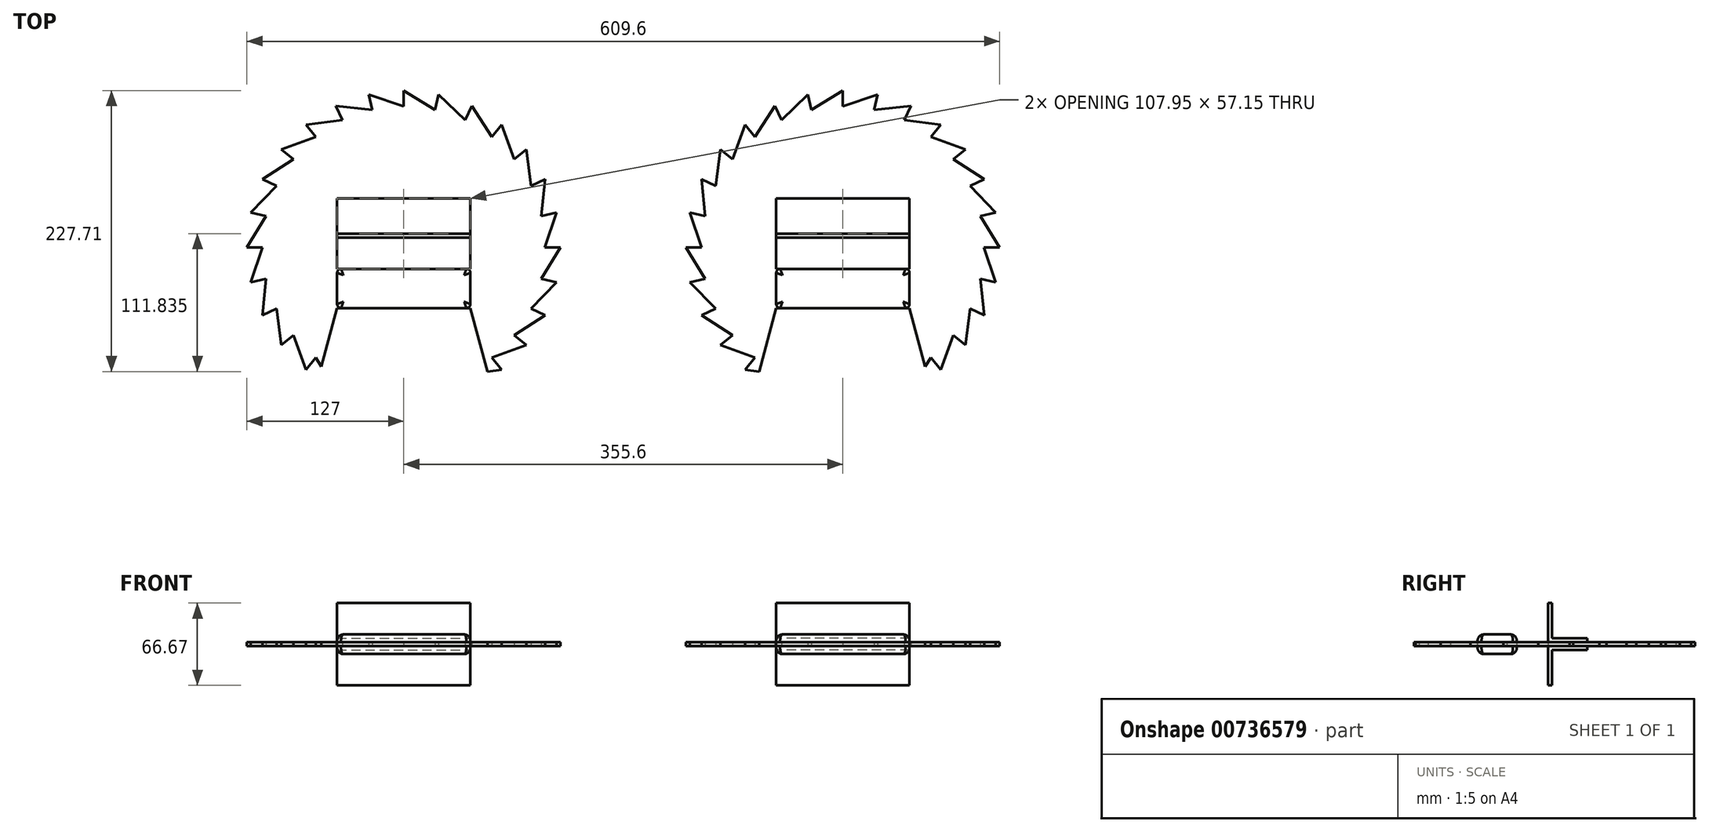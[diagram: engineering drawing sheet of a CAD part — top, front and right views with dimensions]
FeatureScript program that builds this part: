
annotation { "Feature Type Name" : "Feature", "Feature Type Description" : "" }
export const myFeature = defineFeature(function(context is Context, id is Id, definition is map)
    precondition{}
    {
        {
            var Q0;
            Q0=qCreatedBy(makeId("Top.planeOp"),FACE);
            var sketch = newSketch(context, id + "F0", { "sketchPlane" : qUnion([Q0])});
            skArc(sketch, "E0", {"start": v(-123.82, -114.96) * mm, "mid": v(-123.26, -114.7) * mm, "end": v(-122.7, -114.42) * mm, "construction": true});
            skLineSegment(sketch, "E1", {"start": v(-177.8, 114.3) * mm, "end": v(-177.8, 127) * mm});
            skLineSegment(sketch, "E2", {"start": v(-206.06, 123.82) * mm, "end": v(-203.23, 111.43) * mm});
            skLineSegment(sketch, "E3", {"start": v(-232.9, 114.42) * mm, "end": v(-227.4, 102.98) * mm});
            skLineSegment(sketch, "E4", {"start": v(-256.98, 99.3) * mm, "end": v(-249.06, 89.36) * mm});
            skLineSegment(sketch, "E5", {"start": v(-277.1, 79.18) * mm, "end": v(-267.16, 71.27) * mm});
            skLineSegment(sketch, "E6", {"start": v(-292.22, 55.1) * mm, "end": v(-280.78, 49.6) * mm});
            skLineSegment(sketch, "E7", {"start": v(-301.62, 28.26) * mm, "end": v(-289.23, 25.44) * mm});
            skLineSegment(sketch, "E8", {"start": v(-304.8, 0) * mm, "end": v(-292.1, 0) * mm});
            skLineSegment(sketch, "E9", {"start": v(-301.62, -28.26) * mm, "end": v(-289.23, -25.43) * mm});
            skLineSegment(sketch, "E10", {"start": v(-292.22, -55.1) * mm, "end": v(-280.78, -49.6) * mm});
            skLineSegment(sketch, "E11", {"start": v(-277.1, -79.18) * mm, "end": v(-267.17, -71.26) * mm});
            skLineSegment(sketch, "E12", {"start": v(-149.54, 123.82) * mm, "end": v(-152.37, 111.43) * mm});
            skLineSegment(sketch, "E13", {"start": v(-122.7, 114.42) * mm, "end": v(-128.2, 102.98) * mm});
            skLineSegment(sketch, "E14", {"start": v(-98.62, 99.3) * mm, "end": v(-106.54, 89.36) * mm});
            skLineSegment(sketch, "E15", {"start": v(-78.5, 79.18) * mm, "end": v(-88.44, 71.27) * mm});
            skLineSegment(sketch, "E16", {"start": v(-63.38, 55.1) * mm, "end": v(-74.82, 49.6) * mm});
            skLineSegment(sketch, "E17", {"start": v(-53.98, 28.26) * mm, "end": v(-66.37, 25.44) * mm});
            skLineSegment(sketch, "E18", {"start": v(-50.8, 0) * mm, "end": v(-63.5, 0) * mm});
            skLineSegment(sketch, "E19", {"start": v(-53.98, -28.26) * mm, "end": v(-66.37, -25.43) * mm});
            skLineSegment(sketch, "E20", {"start": v(-63.38, -55.1) * mm, "end": v(-74.82, -49.6) * mm});
            skLineSegment(sketch, "E21", {"start": v(-78.5, -79.18) * mm, "end": v(-88.43, -71.26) * mm});
            skLineSegment(sketch, "E22", {"start": v(-98.61, -99.3) * mm, "end": v(-106.53, -89.36) * mm});
            skLineSegment(sketch, "E23", {"start": v(-256.99, -99.3) * mm, "end": v(-249.07, -89.36) * mm});
            skLineSegment(sketch, "E24", {"start": v(-122.7, -114.42) * mm, "end": v(-128.2, -102.98) * mm, "construction": true});
            skLineSegment(sketch, "E25", {"start": v(-110.02, -100.71) * mm, "end": v(-98.61, -99.3) * mm});
            skLineSegment(sketch, "E26", {"start": v(-106.53, -89.36) * mm, "end": v(-78.5, -79.18) * mm});
            skLineSegment(sketch, "E27", {"start": v(-88.43, -71.26) * mm, "end": v(-63.38, -55.1) * mm});
            skLineSegment(sketch, "E28", {"start": v(-74.82, -49.6) * mm, "end": v(-53.98, -28.26) * mm});
            skLineSegment(sketch, "E29", {"start": v(-66.37, -25.43) * mm, "end": v(-50.8, 0) * mm});
            skLineSegment(sketch, "E30", {"start": v(-63.5, 0) * mm, "end": v(-53.98, 28.26) * mm});
            skLineSegment(sketch, "E31", {"start": v(-66.37, 25.44) * mm, "end": v(-63.38, 55.1) * mm});
            skLineSegment(sketch, "E32", {"start": v(-74.82, 49.6) * mm, "end": v(-78.5, 79.18) * mm});
            skLineSegment(sketch, "E33", {"start": v(-88.44, 71.27) * mm, "end": v(-98.62, 99.3) * mm});
            skLineSegment(sketch, "E34", {"start": v(-106.54, 89.36) * mm, "end": v(-122.7, 114.42) * mm});
            skLineSegment(sketch, "E35", {"start": v(-128.2, 102.98) * mm, "end": v(-149.54, 123.82) * mm});
            skLineSegment(sketch, "E36", {"start": v(-152.37, 111.43) * mm, "end": v(-177.8, 127) * mm});
            skLineSegment(sketch, "E37", {"start": v(-177.8, 114.3) * mm, "end": v(-206.06, 123.82) * mm});
            skLineSegment(sketch, "E38", {"start": v(-203.23, 111.43) * mm, "end": v(-232.9, 114.42) * mm});
            skLineSegment(sketch, "E39", {"start": v(-227.4, 102.98) * mm, "end": v(-256.98, 99.3) * mm});
            skLineSegment(sketch, "E40", {"start": v(-249.06, 89.36) * mm, "end": v(-277.1, 79.18) * mm});
            skLineSegment(sketch, "E41", {"start": v(-267.16, 71.27) * mm, "end": v(-292.22, 55.1) * mm});
            skLineSegment(sketch, "E42", {"start": v(-280.78, 49.6) * mm, "end": v(-301.62, 28.26) * mm});
            skLineSegment(sketch, "E43", {"start": v(-289.23, 25.44) * mm, "end": v(-304.8, 0) * mm});
            skLineSegment(sketch, "E44", {"start": v(-292.1, 0) * mm, "end": v(-301.62, -28.26) * mm});
            skLineSegment(sketch, "E45", {"start": v(-289.23, -25.43) * mm, "end": v(-292.22, -55.1) * mm});
            skLineSegment(sketch, "E46", {"start": v(-280.78, -49.6) * mm, "end": v(-277.1, -79.18) * mm});
            skLineSegment(sketch, "E47", {"start": v(-267.17, -71.26) * mm, "end": v(-256.99, -99.3) * mm});
            skLineSegment(sketch, "E48", {"start": v(-249.07, -89.36) * mm, "end": v(-244.45, -96.52) * mm});
            skLineSegment(sketch, "E49", {"start": v(-231.78, 7.95) * mm, "end": v(-123.83, 7.95) * mm});
            skLineSegment(sketch, "E50", {"start": v(-231.78, 7.95) * mm, "end": v(-231.78, -17.45) * mm});
            skLineSegment(sketch, "E51", {"start": v(-123.83, 7.95) * mm, "end": v(-123.83, -17.45) * mm});
            skPoint(sketch, "E52", {"position": v(-123.83, -102.43) * mm});
            skLineSegment(sketch, "E53", {"start": v(-231.78, -17.45) * mm, "end": v(-123.83, -17.45) * mm});
            skLineSegment(sketch, "E54", {"start": v(-231.78, -49.2) * mm, "end": v(-123.83, -49.2) * mm});
            skLineSegment(sketch, "E55", {"start": v(-123.83, -49.2) * mm, "end": v(-97.38, -147.88) * mm});
            skLineSegment(sketch, "E56", {"start": v(-231.78, -49.2) * mm, "end": v(-265.1, -173.6) * mm});
            skPoint(sketch, "E57", {"position": v(-244.45, -96.52) * mm});
            skPoint(sketch, "E58", {"position": v(-110.02, -100.71) * mm});
            skSolve(sketch);
        }
        {
            var Q0;
            Q0=makeQuery(id+"F0.imprint","IMPRINT",FACE,{"disambiguationData":[TD([[makeQuery(id+"F0.imprint","IMPRINT",EDGE,{"derivedFrom":sQuery(id+"F0.wireOp",EDGE,"E1")}),-1.0]])]});
            extrude(context, id + "F1", {"entities" : qUnion([Q0]), "depth" : 3.17 * mm, "offsetDistance" : 25.4 * mm});
        }
        {
            var Q0;
            Q0=qCreatedBy(makeId("Top.planeOp"),FACE);
            var sketch = newSketch(context, id + "F2", { "sketchPlane" : qUnion([Q0])});
            skLineSegment(sketch, "E59.bottom", {"start": v(-228.6, -17.45) * mm, "end": v(-127, -17.45) * mm});
            skLineSegment(sketch, "E59.top", {"start": v(-228.6, -49.2) * mm, "end": v(-127, -49.2) * mm});
            skLineSegment(sketch, "E59.left", {"start": v(-231.78, -20.62) * mm, "end": v(-231.78, -46.02) * mm});
            skLineSegment(sketch, "E59.right", {"start": v(-123.82, -20.62) * mm, "end": v(-123.82, -46.02) * mm});
            skPoint(sketch, "E60.visualSharp", {"position": v(-123.83, -49.2) * mm});
            skArc(sketch, "E60.filletArc", {"start": v(-127, -49.2) * mm, "mid": v(-124.75, -48.27) * mm, "end": v(-123.83, -46.02) * mm});
            skPoint(sketch, "E61.visualSharp", {"position": v(-123.82, -17.45) * mm});
            skArc(sketch, "E61.filletArc", {"start": v(-123.83, -20.62) * mm, "mid": v(-124.75, -18.38) * mm, "end": v(-127, -17.45) * mm});
            skPoint(sketch, "E62.visualSharp", {"position": v(-231.78, -17.45) * mm});
            skArc(sketch, "E62.filletArc", {"start": v(-228.6, -17.45) * mm, "mid": v(-230.85, -18.38) * mm, "end": v(-231.78, -20.62) * mm});
            skPoint(sketch, "E63.visualSharp", {"position": v(-231.78, -49.2) * mm});
            skArc(sketch, "E63.filletArc", {"start": v(-231.78, -46.02) * mm, "mid": v(-230.85, -48.27) * mm, "end": v(-228.6, -49.2) * mm});
            skSolve(sketch);
        }
        {
            var Q0;
            Q0 = qSketchRegion(id + "F2", true);
            extrude(context, id + "F3", {"entities" : qUnion([Q0]), "depth" : 9.52 * mm, "offsetDistance" : 25.4 * mm, "hasSecondDirection" : true, "secondDirectionOppositeDirection" : true, "secondDirectionDepth" : 6.35 * mm});
        }
        {
            var Q0;
            Q0=makeQuery(id+"F3.opExtrude","CAP_FACE",FACE,{"disambiguationData":[OSD([sQuery(id+"F2.wireOp",EDGE,"E59.bottom"),sQuery(id+"F2.wireOp",EDGE,"E59.top"),sQuery(id+"F2.wireOp",EDGE,"E59.left"),sQuery(id+"F2.wireOp",EDGE,"E59.right"),sQuery(id+"F2.wireOp",EDGE,"E60.filletArc"),sQuery(id+"F2.wireOp",EDGE,"E61.filletArc"),sQuery(id+"F2.wireOp",EDGE,"E62.filletArc"),sQuery(id+"F2.wireOp",EDGE,"E63.filletArc")])],"isStart":true});
            var Q1;
            Q1=makeQuery(id+"F3.opExtrude","CAP_FACE",FACE,{"disambiguationData":[OSD([sQuery(id+"F2.wireOp",EDGE,"E59.bottom"),sQuery(id+"F2.wireOp",EDGE,"E59.top"),sQuery(id+"F2.wireOp",EDGE,"E59.left"),sQuery(id+"F2.wireOp",EDGE,"E59.right"),sQuery(id+"F2.wireOp",EDGE,"E60.filletArc"),sQuery(id+"F2.wireOp",EDGE,"E61.filletArc"),sQuery(id+"F2.wireOp",EDGE,"E62.filletArc"),sQuery(id+"F2.wireOp",EDGE,"E63.filletArc")])],"isStart":false});
            fillet(context, id + "F4", {"entities" : qUnion([Q0, Q1]), "radius" : 5.08 * mm, "tangentPropagation" : true, "allowEdgeOverflow" : false});
        }
        {
            var Q0;
            Q0=qCreatedBy(makeId("Right.planeOp"),FACE);
            var sketch = newSketch(context, id + "F5", { "sketchPlane" : qUnion([Q0])});
            skLineSegment(sketch, "E64.bottom", {"start": v(7.95, 34.93) * mm, "end": v(11.13, 34.93) * mm});
            skLineSegment(sketch, "E64.top", {"start": v(7.95, 3.18) * mm, "end": v(39.7, 3.18) * mm});
            skLineSegment(sketch, "E64.left", {"start": v(7.95, 34.93) * mm, "end": v(7.95, 3.18) * mm});
            skLineSegment(sketch, "E64.right", {"start": v(39.7, 6.35) * mm, "end": v(39.7, 3.18) * mm});
            skLineSegment(sketch, "E65", {"start": v(11.13, 34.92) * mm, "end": v(11.13, 6.35) * mm});
            skLineSegment(sketch, "E66", {"start": v(11.13, 6.35) * mm, "end": v(39.7, 6.35) * mm});
            skLineSegment(sketch, "E67", {"start": v(147.17, 0) * mm, "end": v(-127.53, 0) * mm, "construction": true});
            skLineSegment(sketch, "E68.MirrorCS", {"start": v(7.95, 0) * mm, "end": v(39.7, 0) * mm});
            skLineSegment(sketch, "E69.MirrorCS", {"start": v(11.13, -3.17) * mm, "end": v(39.7, -3.17) * mm});
            skLineSegment(sketch, "E70.MirrorCS", {"start": v(39.7, -3.17) * mm, "end": v(39.7, 0) * mm});
            skLineSegment(sketch, "E71.MirrorCS", {"start": v(7.95, -31.75) * mm, "end": v(7.95, 0) * mm});
            skLineSegment(sketch, "E72.MirrorCS", {"start": v(11.13, -31.75) * mm, "end": v(11.13, -3.17) * mm});
            skLineSegment(sketch, "E73.MirrorCS", {"start": v(7.95, -31.75) * mm, "end": v(11.13, -31.75) * mm});
            skSolve(sketch);
        }
        {
            var Q0;
            Q0 = qSketchRegion(id + "F5", true);
            extrude(context, id + "F6", {"entities" : qUnion([Q0]), "operationType" : NewBodyOperationType.ADD, "oppositeDirection" : true, "depth" : 231.77 * mm, "offsetDistance" : 25.4 * mm, "hasSecondDirection" : true, "secondDirectionOppositeDirection" : true, "secondDirectionDepth" : 123.82 * mm});
        }
        {
            var Q0;
            Q0=makeQuery(id+"F1.opExtrude","SWEPT_BODY",BODY,{"disambiguationData":[OSD([sQuery(id+"F0.wireOp",EDGE,"E1"),sQuery(id+"F0.wireOp",EDGE,"E2"),sQuery(id+"F0.wireOp",EDGE,"E3"),sQuery(id+"F0.wireOp",EDGE,"E4"),sQuery(id+"F0.wireOp",EDGE,"E5"),sQuery(id+"F0.wireOp",EDGE,"E6"),sQuery(id+"F0.wireOp",EDGE,"E7"),sQuery(id+"F0.wireOp",EDGE,"E8"),sQuery(id+"F0.wireOp",EDGE,"E9"),sQuery(id+"F0.wireOp",EDGE,"E10"),sQuery(id+"F0.wireOp",EDGE,"E11"),sQuery(id+"F0.wireOp",EDGE,"E12"),sQuery(id+"F0.wireOp",EDGE,"E13"),sQuery(id+"F0.wireOp",EDGE,"E14"),sQuery(id+"F0.wireOp",EDGE,"E15"),sQuery(id+"F0.wireOp",EDGE,"E16"),sQuery(id+"F0.wireOp",EDGE,"E17"),sQuery(id+"F0.wireOp",EDGE,"E18"),sQuery(id+"F0.wireOp",EDGE,"E19"),sQuery(id+"F0.wireOp",EDGE,"E20"),sQuery(id+"F0.wireOp",EDGE,"E21"),sQuery(id+"F0.wireOp",EDGE,"E22"),sQuery(id+"F0.wireOp",EDGE,"E23"),sQuery(id+"F0.wireOp",EDGE,"E25"),sQuery(id+"F0.wireOp",EDGE,"E26"),sQuery(id+"F0.wireOp",EDGE,"E27"),sQuery(id+"F0.wireOp",EDGE,"E28"),sQuery(id+"F0.wireOp",EDGE,"E29"),sQuery(id+"F0.wireOp",EDGE,"E30"),sQuery(id+"F0.wireOp",EDGE,"E31"),sQuery(id+"F0.wireOp",EDGE,"E32"),sQuery(id+"F0.wireOp",EDGE,"E33"),sQuery(id+"F0.wireOp",EDGE,"E34"),sQuery(id+"F0.wireOp",EDGE,"E35"),sQuery(id+"F0.wireOp",EDGE,"E36"),sQuery(id+"F0.wireOp",EDGE,"E37"),sQuery(id+"F0.wireOp",EDGE,"E38"),sQuery(id+"F0.wireOp",EDGE,"E39"),sQuery(id+"F0.wireOp",EDGE,"E40"),sQuery(id+"F0.wireOp",EDGE,"E41"),sQuery(id+"F0.wireOp",EDGE,"E42"),sQuery(id+"F0.wireOp",EDGE,"E43"),sQuery(id+"F0.wireOp",EDGE,"E44"),sQuery(id+"F0.wireOp",EDGE,"E45"),sQuery(id+"F0.wireOp",EDGE,"E46"),sQuery(id+"F0.wireOp",EDGE,"E47"),sQuery(id+"F0.wireOp",EDGE,"E48"),sQuery(id+"F0.wireOp",EDGE,"E49"),sQuery(id+"F0.wireOp",EDGE,"E50"),sQuery(id+"F0.wireOp",EDGE,"E51"),sQuery(id+"F0.wireOp",EDGE,"E53"),sQuery(id+"F0.wireOp",EDGE,"E54"),sQuery(id+"F0.wireOp",EDGE,"E55"),sQuery(id+"F0.wireOp",EDGE,"E56")])]});
            var Q1;
            Q1=makeQuery(id+"F3.opExtrude","SWEPT_BODY",BODY,{"disambiguationData":[OSD([sQuery(id+"F2.wireOp",EDGE,"E59.bottom"),sQuery(id+"F2.wireOp",EDGE,"E59.top"),sQuery(id+"F2.wireOp",EDGE,"E59.left"),sQuery(id+"F2.wireOp",EDGE,"E59.right"),sQuery(id+"F2.wireOp",EDGE,"E60.filletArc"),sQuery(id+"F2.wireOp",EDGE,"E61.filletArc"),sQuery(id+"F2.wireOp",EDGE,"E62.filletArc"),sQuery(id+"F2.wireOp",EDGE,"E63.filletArc")])]});
            var Q2;
            Q2=qCreatedBy(makeId("Right.planeOp"),FACE);
            mirror(context, id + "F7", {"entities" : qUnion([Q0, Q1]), "mirrorPlane" : qUnion([Q2])});
        }
    });
